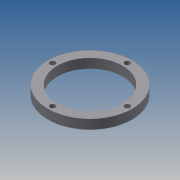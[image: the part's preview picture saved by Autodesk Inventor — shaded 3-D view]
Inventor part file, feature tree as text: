
AUTODESK INVENTOR PART (.ipt)
format: ipt  version: 2013 (Build 170138000, 138)  size: 120,832 bytes
history: native  units: mm
features: extrude x3, sketch x3, pattern_circular x1
ambient origin geometry x8: Origin, YZ Plane, XZ Plane, XY Plane, X Axis, Y Axis, Z Axis, Center Point
bodies: Solid1 (feature_tree)
feature tree (7):
  extrude  "Extrusion1"  Depth=90.0mm
  extrude  "Extrusion2"  Depth=40.0mm
  extrude  "Extrusion3"  Depth=10.0mm TaperAngle=0.0deg
  pattern_circular  "Circular Pattern1"  [2 undecoded]
  sketch  "Sketch1"  dims[d0=70.0mm d2=90.0mm]
  sketch  "Sketch2"  dims[d3=10.0mm d4=0.0mm d5=40.0mm]
  sketch  "Sketch3"  dims[d6=3.5mm d7=10.0mm d8=0.0mm d9=5.5mm d10=4.0mm d11=0.0mm d12=40.0mm d13=360.0deg]
note: 2 required parameter values undecoded (feature->parameter linkage not recoverable at this tier; creation-order binding heuristic only, values carry confidence <= 0.55)
